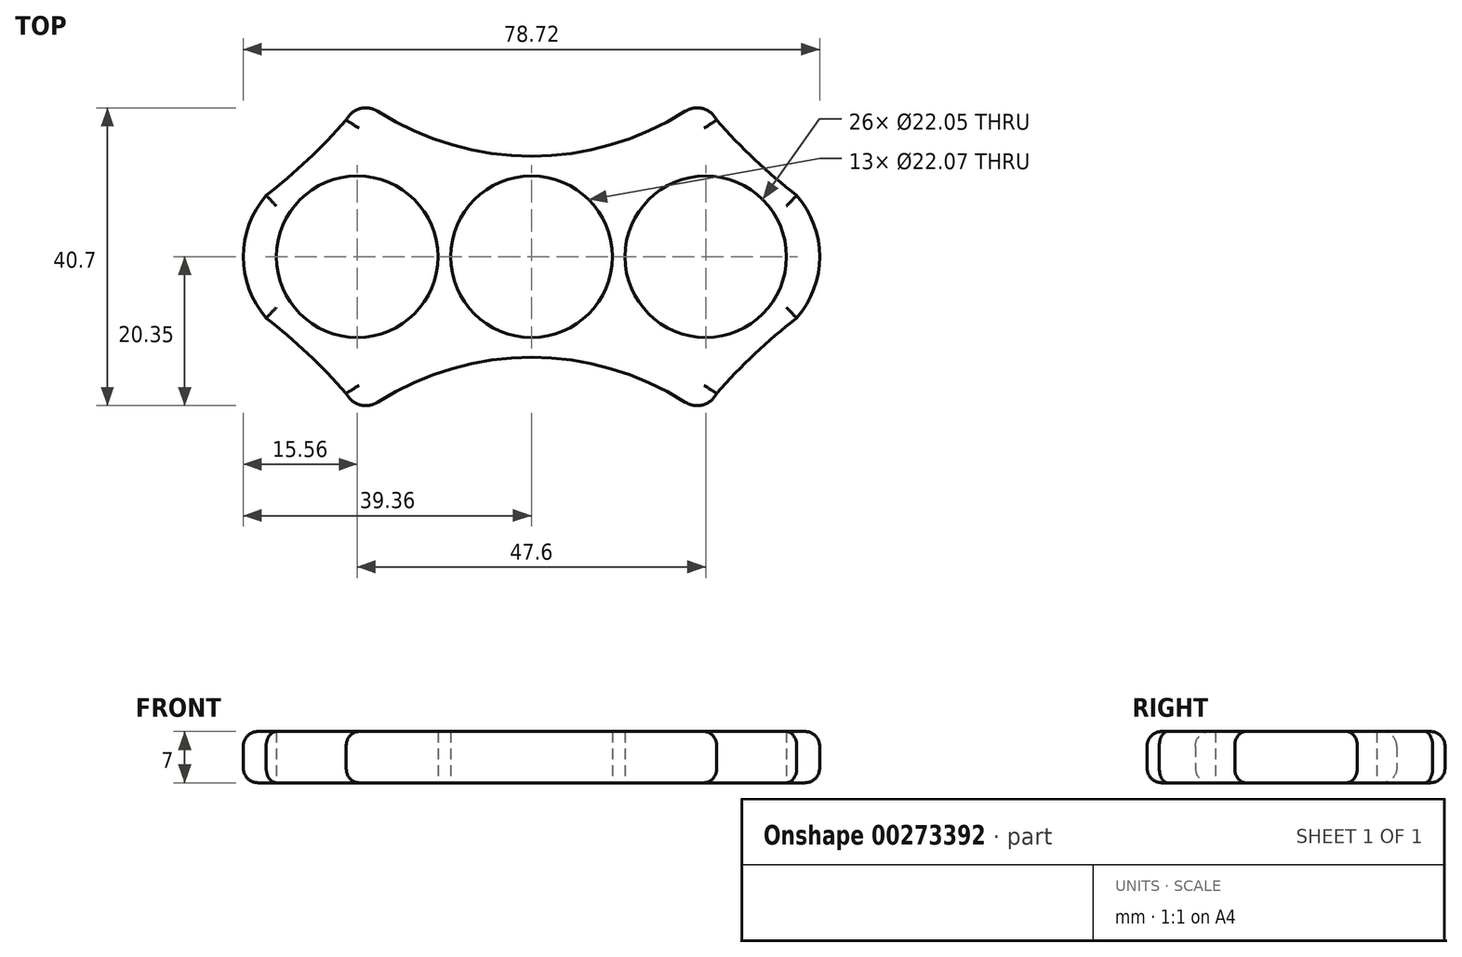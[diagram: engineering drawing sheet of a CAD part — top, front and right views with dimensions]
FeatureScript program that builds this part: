
annotation { "Feature Type Name" : "Feature", "Feature Type Description" : "" }
export const myFeature = defineFeature(function(context is Context, id is Id, definition is map)
    precondition{}
    {
        {
            var Q0;
            Q0=qCreatedBy(makeId("Top.planeOp"),FACE);
            var sketch = newSketch(context, id + "F0", { "sketchPlane" : qUnion([Q0])});
            skCircle(sketch, "E0", {"center": v(0, 0) * mm, "radius": 11.04 * mm});
            skPoint(sketch, "E1.orphan", {"position": v(11.51, -11.4) * mm});
            skPoint(sketch, "E2.visualSharp", {"position": v(-24, 21) * mm});
            skPoint(sketch, "E3.MirrorCS.end.orphan", {"position": v(19.74, -18.06) * mm});
            skPoint(sketch, "E3.MirrorCS.start.orphan", {"position": v(26.37, -16.66) * mm});
            skArc(sketch, "E4", {"start": v(-21, 19.88) * mm, "mid": v(0, 13.74) * mm, "end": v(21, 19.88) * mm});
            skPoint(sketch, "E5.visualSharp", {"position": v(-24, 22) * mm});
            skArc(sketch, "E5.filletArc", {"start": v(-21, 19.88) * mm, "mid": v(-23.42, 20.24) * mm, "end": v(-25.3, 18.67) * mm});
            skPoint(sketch, "E6.visualSharp", {"position": v(24, 22) * mm});
            skArc(sketch, "E6.filletArc", {"start": v(25.3, 18.67) * mm, "mid": v(23.42, 20.24) * mm, "end": v(21, 19.88) * mm});
            skArc(sketch, "E7.MirrorCS", {"start": v(-21, -19.88) * mm, "mid": v(0, -13.74) * mm, "end": v(21, -19.88) * mm});
            skArc(sketch, "E8.MirrorCS", {"start": v(25.3, -18.67) * mm, "mid": v(23.42, -20.24) * mm, "end": v(21, -19.88) * mm});
            skArc(sketch, "E9.MirrorCS", {"start": v(-21, -19.88) * mm, "mid": v(-23.42, -20.24) * mm, "end": v(-25.3, -18.67) * mm});
            skCircle(sketch, "E10", {"center": v(-23.8, 0) * mm, "radius": 11.03 * mm});
            skLineSegment(sketch, "E11", {"start": v(0, 0) * mm, "end": v(0, 11.04) * mm, "construction": true});
            skArc(sketch, "E12", {"start": v(-36.23, 8.37) * mm, "mid": v(-39.36, 0) * mm, "end": v(-36.23, -8.37) * mm});
            skArc(sketch, "E13", {"start": v(-36.23, 8.37) * mm, "mid": v(-30.52, 13.26) * mm, "end": v(-25.3, 18.67) * mm});
            skLineSegment(sketch, "E14", {"start": v(-23.8, 0) * mm, "end": v(0, 0) * mm, "construction": true});
            skArc(sketch, "E15.MirrorCS", {"start": v(-36.23, -8.37) * mm, "mid": v(-30.52, -13.26) * mm, "end": v(-25.3, -18.67) * mm});
            skArc(sketch, "E16.MirrorCS", {"start": v(36.23, -8.37) * mm, "mid": v(30.52, -13.26) * mm, "end": v(25.3, -18.67) * mm});
            skArc(sketch, "E17.MirrorCS", {"start": v(36.23, 8.37) * mm, "mid": v(30.52, 13.26) * mm, "end": v(25.3, 18.67) * mm});
            skCircle(sketch, "E18.MirrorC", {"center": v(23.8, 0) * mm, "radius": 11.03 * mm});
            skArc(sketch, "E19.MirrorCS", {"start": v(36.23, 8.37) * mm, "mid": v(39.36, 0) * mm, "end": v(36.23, -8.37) * mm});
            skSolve(sketch);
        }
        {
            var Q0;
            Q0=makeQuery(id+"F0.imprint","IMPRINT",FACE,{"disambiguationData":[TD([[makeQuery(id+"F0.imprint","IMPRINT",EDGE,{"derivedFrom":sQuery(id+"F0.wireOp",EDGE,"E0")}),-1.0]])]});
            var Q1;
            {var subQ3=sQuery(id+"F0.wireOp",EDGE,"3ZWXOmwt-CgLn-e10W-X5N8-Iw0rjgBFTwU5");Q1=makeQuery(id+"F0.imprint","IMPRINT",FACE,{"disambiguationData":[TD([[makeQuery(id+"F0.imprint","IMPRINT",EDGE,{"derivedFrom":subQ3}),-1.0]])]});}
            var Q2;
            {var subQ3=sQuery(id+"F0.wireOp",EDGE,"3dd6d1d2-8736-4229-b16c-4bedbf3db8470.MirrorCS");Q2=makeQuery(id+"F0.imprint","IMPRINT",FACE,{"disambiguationData":[TD([[makeQuery(id+"F0.imprint","IMPRINT",EDGE,{"derivedFrom":subQ3}),1.0]])]});}
            extrude(context, id + "F1", {"entities" : qUnion([Q0, Q1, Q2]), "depth" : 7 * mm});
        }
        {
            var Q0;
            Q0=makeQuery(id+"F1.opExtrude","CAP_EDGE",EDGE,{"disambiguationData":[OSD([sQuery(id+"F0.wireOp",EDGE,"E12")])],"isStart":false});
            var Q1;
            Q1=makeQuery(id+"F1.opExtrude","CAP_EDGE",EDGE,{"disambiguationData":[OSD([sQuery(id+"F0.wireOp",EDGE,"E13")])],"isStart":false});
            var Q2;
            Q2=makeQuery(id+"F1.opExtrude","CAP_EDGE",EDGE,{"disambiguationData":[OSD([sQuery(id+"F0.wireOp",EDGE,"E5.filletArc")])],"isStart":false});
            var Q3;
            Q3=makeQuery(id+"F1.opExtrude","CAP_EDGE",EDGE,{"disambiguationData":[OSD([sQuery(id+"F0.wireOp",EDGE,"E4")])],"isStart":false});
            var Q4;
            Q4=makeQuery(id+"F1.opExtrude","CAP_EDGE",EDGE,{"disambiguationData":[OSD([sQuery(id+"F0.wireOp",EDGE,"E6.filletArc")])],"isStart":false});
            var Q5;
            Q5=makeQuery(id+"F1.opExtrude","CAP_EDGE",EDGE,{"disambiguationData":[OSD([sQuery(id+"F0.wireOp",EDGE,"E17.MirrorCS")])],"isStart":false});
            var Q6;
            Q6=makeQuery(id+"F1.opExtrude","CAP_EDGE",EDGE,{"disambiguationData":[OSD([sQuery(id+"F0.wireOp",EDGE,"E16.MirrorCS")])],"isStart":false});
            var Q7;
            Q7=makeQuery(id+"F1.opExtrude","CAP_EDGE",EDGE,{"disambiguationData":[OSD([sQuery(id+"F0.wireOp",EDGE,"E7.MirrorCS")])],"isStart":false});
            var Q8;
            Q8=makeQuery(id+"F1.opExtrude","CAP_EDGE",EDGE,{"disambiguationData":[OSD([sQuery(id+"F0.wireOp",EDGE,"E15.MirrorCS")])],"isStart":false});
            var Q9;
            Q9=makeQuery(id+"F1.opExtrude","CAP_EDGE",EDGE,{"disambiguationData":[OSD([sQuery(id+"F0.wireOp",EDGE,"E12")])],"isStart":true});
            var Q10;
            Q10=makeQuery(id+"F1.opExtrude","CAP_EDGE",EDGE,{"disambiguationData":[OSD([sQuery(id+"F0.wireOp",EDGE,"E15.MirrorCS")])],"isStart":true});
            var Q11;
            Q11=makeQuery(id+"F1.opExtrude","CAP_EDGE",EDGE,{"disambiguationData":[OSD([sQuery(id+"F0.wireOp",EDGE,"E9.MirrorCS")])],"isStart":true});
            var Q12;
            Q12=makeQuery(id+"F1.opExtrude","CAP_EDGE",EDGE,{"disambiguationData":[OSD([sQuery(id+"F0.wireOp",EDGE,"E9.MirrorCS")])],"isStart":false});
            var Q13;
            Q13=makeQuery(id+"F1.opExtrude","CAP_EDGE",EDGE,{"disambiguationData":[OSD([sQuery(id+"F0.wireOp",EDGE,"E8.MirrorCS")])],"isStart":false});
            var Q14;
            Q14=makeQuery(id+"F1.opExtrude","CAP_EDGE",EDGE,{"disambiguationData":[OSD([sQuery(id+"F0.wireOp",EDGE,"E7.MirrorCS")])],"isStart":true});
            var Q15;
            Q15=makeQuery(id+"F1.opExtrude","CAP_EDGE",EDGE,{"disambiguationData":[OSD([sQuery(id+"F0.wireOp",EDGE,"E16.MirrorCS")])],"isStart":true});
            var Q16;
            Q16=makeQuery(id+"F1.opExtrude","CAP_EDGE",EDGE,{"disambiguationData":[OSD([sQuery(id+"F0.wireOp",EDGE,"E13")])],"isStart":true});
            var Q17;
            Q17=makeQuery(id+"F1.opExtrude","CAP_EDGE",EDGE,{"disambiguationData":[OSD([sQuery(id+"F0.wireOp",EDGE,"E4")])],"isStart":true});
            var Q18;
            Q18=makeQuery(id+"F1.opExtrude","CAP_EDGE",EDGE,{"disambiguationData":[OSD([sQuery(id+"F0.wireOp",EDGE,"E6.filletArc")])],"isStart":true});
            var Q19;
            Q19=makeQuery(id+"F1.opExtrude","CAP_EDGE",EDGE,{"disambiguationData":[OSD([sQuery(id+"F0.wireOp",EDGE,"E17.MirrorCS")])],"isStart":true});
            var Q20;
            Q20=makeQuery(id+"F1.opExtrude","CAP_EDGE",EDGE,{"disambiguationData":[OSD([sQuery(id+"F0.wireOp",EDGE,"E19.MirrorCS")])],"isStart":true});
            var Q21;
            Q21=makeQuery(id+"F1.opExtrude","CAP_EDGE",EDGE,{"disambiguationData":[OSD([sQuery(id+"F0.wireOp",EDGE,"E19.MirrorCS")])],"isStart":false});
            fillet(context, id + "F2", {"entities" : qUnion([Q0, Q1, Q2, Q3, Q4, Q5, Q6, Q7, Q8, Q9, Q10, Q11, Q12, Q13, Q14, Q15, Q16, Q17, Q18, Q19, Q20, Q21]), "radius" : 2 * mm, "tangentPropagation" : true, "allowEdgeOverflow" : false});
        }
    });
